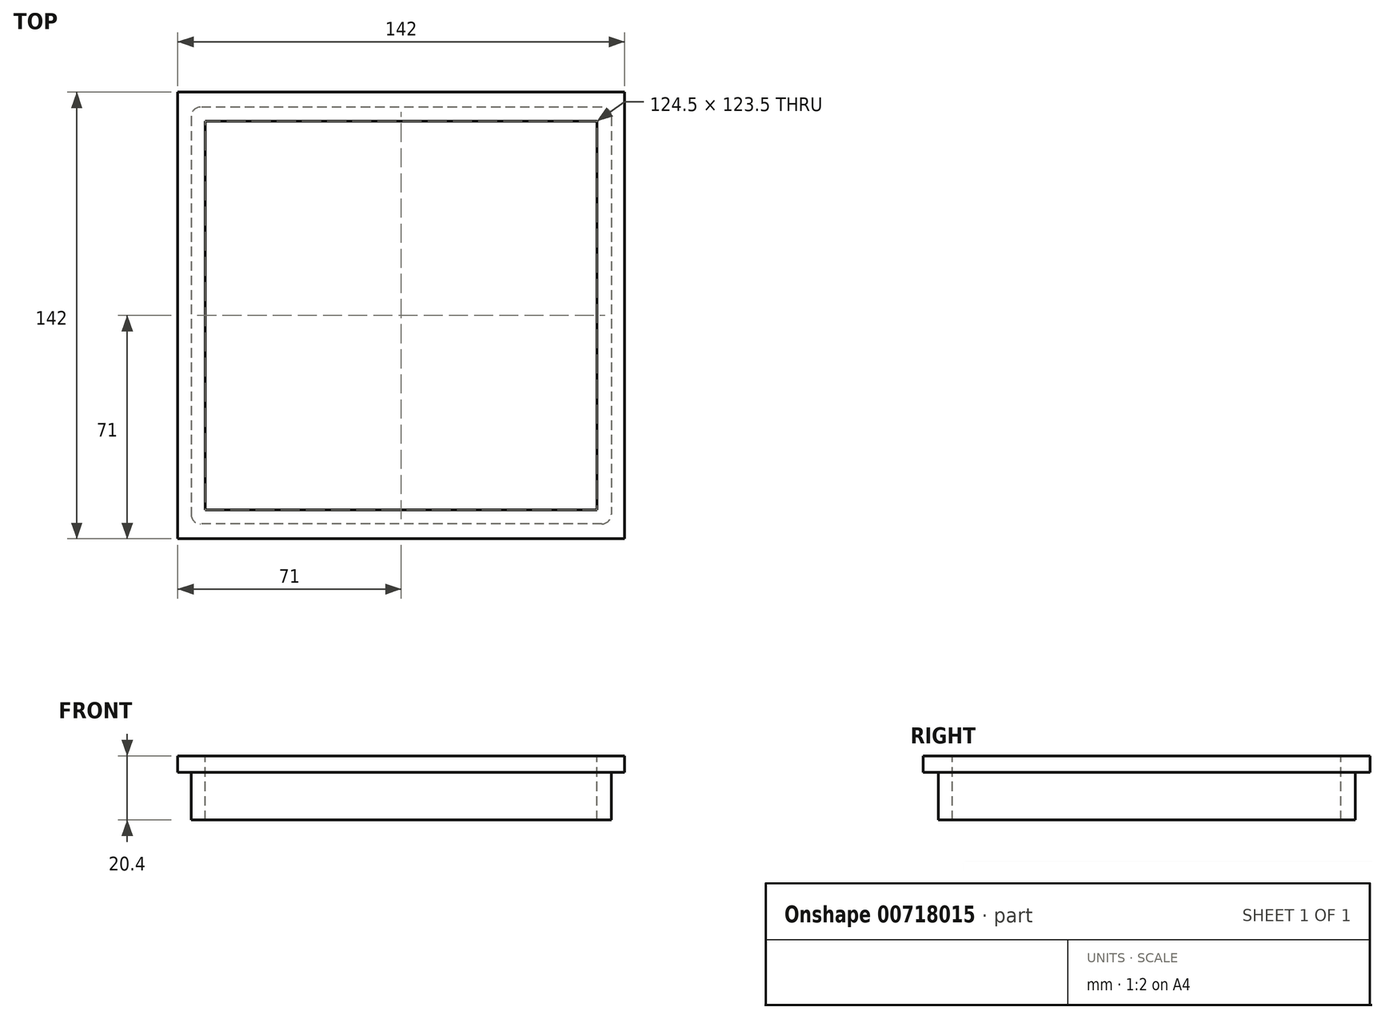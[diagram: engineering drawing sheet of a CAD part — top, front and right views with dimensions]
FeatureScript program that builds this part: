
annotation { "Feature Type Name" : "Feature", "Feature Type Description" : "" }
export const myFeature = defineFeature(function(context is Context, id is Id, definition is map)
    precondition{}
    {
        {
            var Q0;
            Q0=qCreatedBy(makeId("Top.planeOp"),FACE);
            var sketch = newSketch(context, id + "F0", { "sketchPlane" : qUnion([Q0])});
            skLineSegment(sketch, "E0.bottom", {"start": v(71, 71) * mm, "end": v(-71, 71) * mm});
            skLineSegment(sketch, "E0.top", {"start": v(71, -71) * mm, "end": v(-71, -71) * mm});
            skLineSegment(sketch, "E0.left", {"start": v(71, 71) * mm, "end": v(71, -71) * mm});
            skLineSegment(sketch, "E0.right", {"start": v(-71, 71) * mm, "end": v(-71, -71) * mm});
            skLineSegment(sketch, "E1.bottom", {"start": v(63.75, 66.25) * mm, "end": v(-63.75, 66.25) * mm});
            skLineSegment(sketch, "E1.top", {"start": v(63.75, -66.25) * mm, "end": v(-63.75, -66.25) * mm});
            skLineSegment(sketch, "E1.left", {"start": v(66.75, 63.25) * mm, "end": v(66.75, -63.25) * mm});
            skLineSegment(sketch, "E1.right", {"start": v(-66.75, 63.25) * mm, "end": v(-66.75, -63.25) * mm});
            skPoint(sketch, "E1.middle", {"position": v(0, 0) * mm});
            skLineSegment(sketch, "E2.0", {"start": v(-62.25, 61.75) * mm, "end": v(-62.25, -61.75) * mm});
            skLineSegment(sketch, "E2.1", {"start": v(62.25, 61.75) * mm, "end": v(-62.25, 61.75) * mm});
            skLineSegment(sketch, "E2.2", {"start": v(62.25, 61.75) * mm, "end": v(62.25, -61.75) * mm});
            skLineSegment(sketch, "E2.3", {"start": v(62.25, -61.75) * mm, "end": v(-62.25, -61.75) * mm});
            skPoint(sketch, "E3.visualSharp", {"position": v(66.75, 66.25) * mm});
            skArc(sketch, "E3.filletArc", {"start": v(66.75, 64.25) * mm, "mid": v(66.16, 65.66) * mm, "end": v(64.75, 66.25) * mm});
            skArc(sketch, "E4.filletArc", {"start": v(66.75, 63.25) * mm, "mid": v(65.87, 65.37) * mm, "end": v(63.75, 66.25) * mm});
            skPoint(sketch, "E5.visualSharp", {"position": v(66.75, -66.25) * mm});
            skArc(sketch, "E5.filletArc", {"start": v(63.75, -66.25) * mm, "mid": v(65.87, -65.37) * mm, "end": v(66.75, -63.25) * mm});
            skPoint(sketch, "E6.visualSharp", {"position": v(-66.75, -66.25) * mm});
            skArc(sketch, "E6.filletArc", {"start": v(-66.75, -63.25) * mm, "mid": v(-65.87, -65.37) * mm, "end": v(-63.75, -66.25) * mm});
            skPoint(sketch, "E7.visualSharp", {"position": v(-66.75, 66.25) * mm});
            skArc(sketch, "E7.filletArc", {"start": v(-63.75, 66.25) * mm, "mid": v(-65.87, 65.37) * mm, "end": v(-66.75, 63.25) * mm});
            skSolve(sketch);
        }
        {
            var Q0;
            Q0=makeQuery(id+"F0.imprint","IMPRINT",FACE,{"disambiguationData":[TD([[makeQuery(id+"F0.imprint","IMPRINT",EDGE,{"derivedFrom":sQuery(id+"F0.wireOp",EDGE,"E0.bottom")}),1.0]])]});
            extrude(context, id + "F1", {"entities" : qUnion([Q0]), "oppositeDirection" : true, "depth" : 5.2 * mm, "offsetDistance" : 25 * mm});
        }
        {
            var Q0;
            Q0=makeQuery(id+"F0.imprint","IMPRINT",FACE,{"disambiguationData":[TD([[makeQuery(id+"F0.imprint","IMPRINT",EDGE,{"derivedFrom":sQuery(id+"F0.wireOp",EDGE,"E1.bottom")}),1.0]])]});
            extrude(context, id + "F2", {"entities" : qUnion([Q0]), "operationType" : NewBodyOperationType.ADD, "oppositeDirection" : true, "depth" : 20.4 * mm, "offsetDistance" : 25 * mm});
        }
    });
